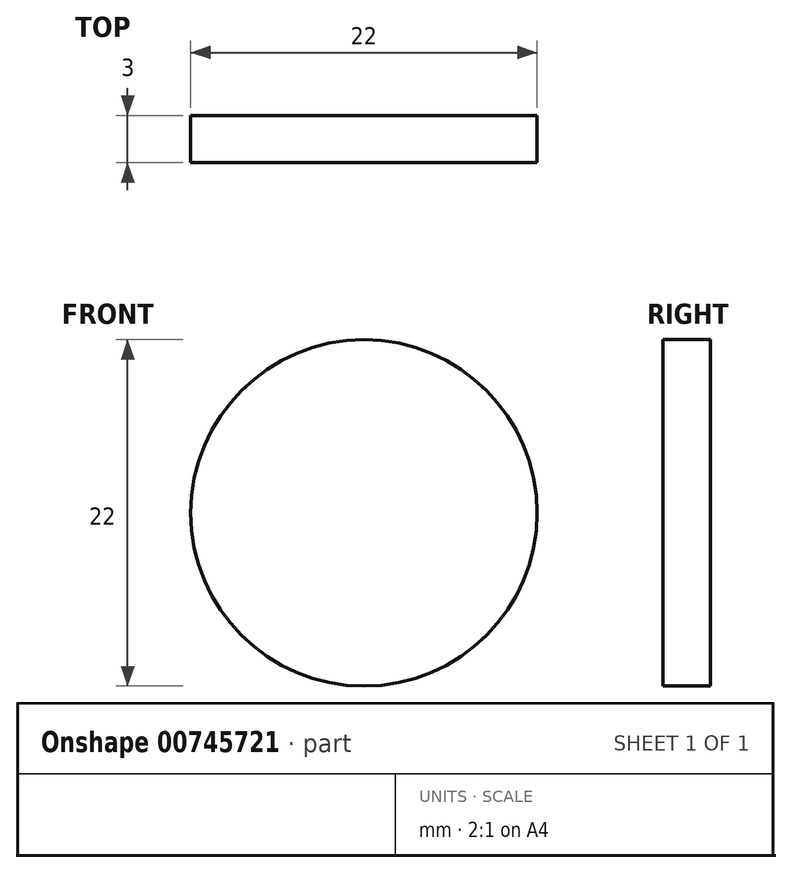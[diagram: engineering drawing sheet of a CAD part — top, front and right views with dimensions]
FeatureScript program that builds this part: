
annotation { "Feature Type Name" : "Feature", "Feature Type Description" : "" }
export const myFeature = defineFeature(function(context is Context, id is Id, definition is map)
    precondition{}
    {
        {
            var Q0;
            Q0=qCreatedBy(makeId("Front.planeOp"),FACE);
            var sketch = newSketch(context, id + "F0", { "sketchPlane" : qUnion([Q0])});
            skCircle(sketch, "E0", {"center": v(0, 0) * mm, "radius": 11 * mm});
            skSolve(sketch);
        }
        {
            var Q0;
            Q0 = qSketchRegion(id + "F0", true);
            extrude(context, id + "F1", {"entities" : qUnion([Q0]), "depth" : 3 * mm, "offsetDistance" : 25 * mm});
        }
    });
